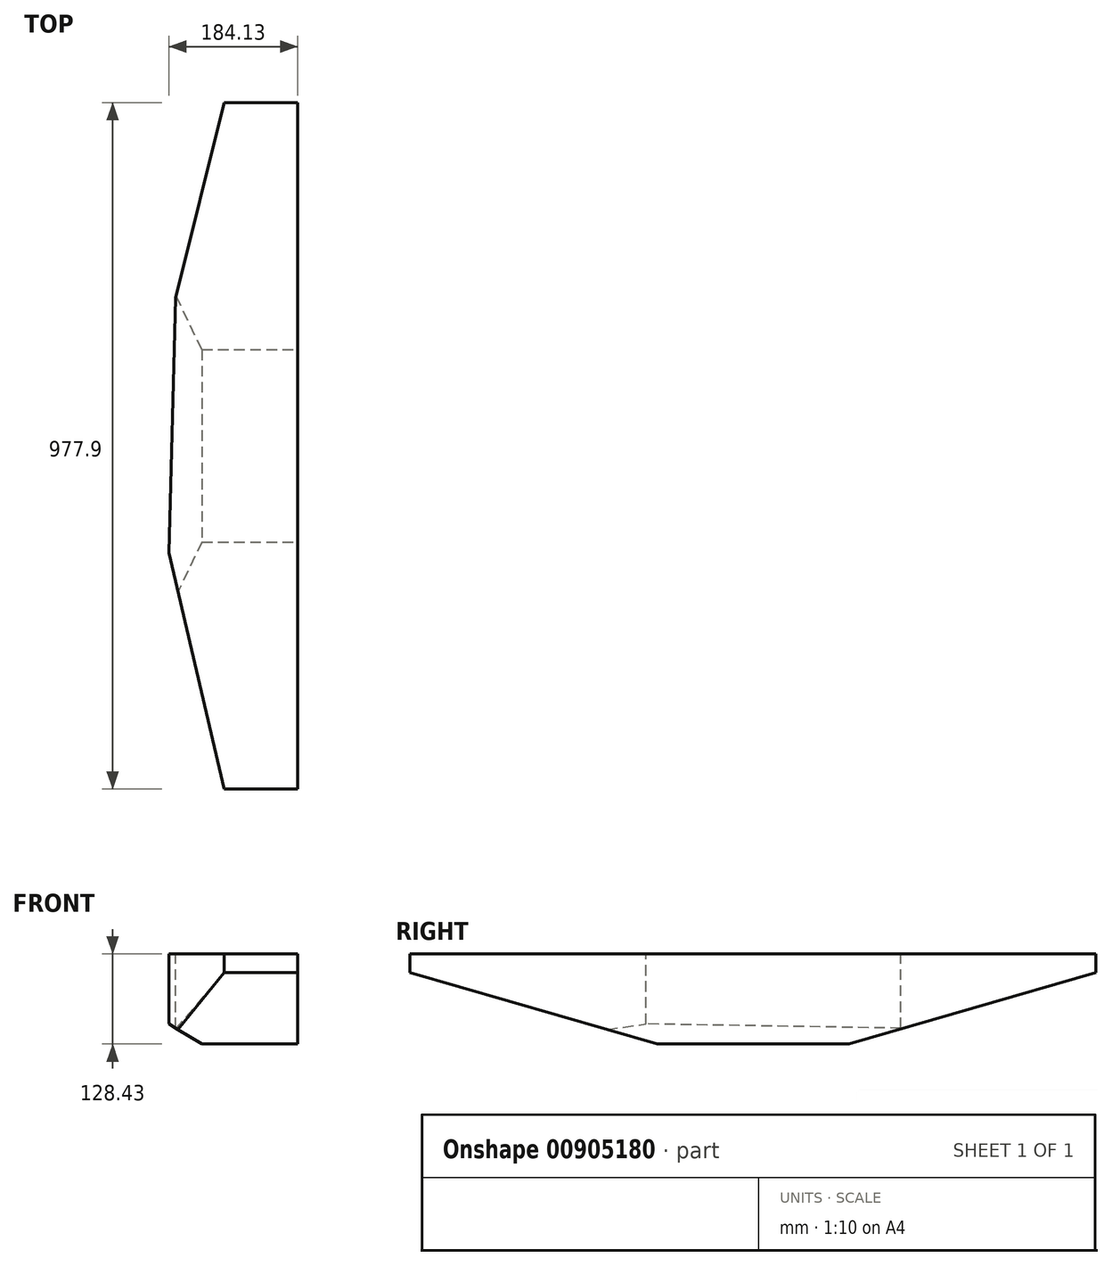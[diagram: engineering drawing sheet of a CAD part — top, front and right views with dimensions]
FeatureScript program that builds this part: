
annotation { "Feature Type Name" : "Feature", "Feature Type Description" : "" }
export const myFeature = defineFeature(function(context is Context, id is Id, definition is map)
    precondition{}
    {
        {
            var Q0;
            Q0=qCreatedBy(makeId("Front.planeOp"),FACE);
            var sketch = newSketch(context, id + "F0", { "sketchPlane" : qUnion([Q0])});
            skLineSegment(sketch, "E0", {"start": v(0, 0) * mm, "end": v(-306, 0) * mm});
            skLineSegment(sketch, "E1", {"start": v(-306, 0) * mm, "end": v(-306, 128.43) * mm});
            skLineSegment(sketch, "E2", {"start": v(-306, 128.43) * mm, "end": v(0, 128.43) * mm});
            skLineSegment(sketch, "E3", {"start": v(0, 128.43) * mm, "end": v(0, 0) * mm});
            skSolve(sketch);
        }
        {
            var Q0;
            Q0 = qSketchRegion(id + "F0", true);
            extrude(context, id + "F1", {"entities" : qUnion([Q0]), "depth" : 977.9 * mm, "offsetDistance" : 25.4 * mm});
        }
        {
            var Q0;
            Q0=makeQuery(id+"F1.opExtrude","SWEPT_FACE",FACE,{"disambiguationData":[OSD([sQuery(id+"F0.wireOp",EDGE,"E3")])]});
            var sketch = newSketch(context, id + "F2", { "sketchPlane" : qUnion([Q0])});
            skLineSegment(sketch, "E4", {"start": v(-977.9, 102.12) * mm, "end": v(-625.85, 0) * mm});
            skLineSegment(sketch, "E5", {"start": v(-625.85, 0) * mm, "end": v(-977.9, 0) * mm});
            skLineSegment(sketch, "E6", {"start": v(-977.9, 0) * mm, "end": v(-977.9, 102.12) * mm});
            skLineSegment(sketch, "E7", {"start": v(0, 0) * mm, "end": v(0, 102.12) * mm});
            skLineSegment(sketch, "E8", {"start": v(0, 102.12) * mm, "end": v(-352.04, 0) * mm});
            skLineSegment(sketch, "E9", {"start": v(-352.04, 0) * mm, "end": v(0, 0) * mm});
            skSolve(sketch);
        }
        {
            var Q0;
            Q0 = qSketchRegion(id + "F2", true);
            extrude(context, id + "F3", {"entities" : qUnion([Q0]), "operationType" : NewBodyOperationType.REMOVE, "oppositeDirection" : true, "depth" : 508 * mm, "offsetDistance" : 25.4 * mm});
        }
        {
            var Q0;
            Q0=makeQuery(id+"F1.opExtrude","CAP_FACE",FACE,{"disambiguationData":[OSD([sQuery(id+"F0.wireOp",EDGE,"E0"),sQuery(id+"F0.wireOp",EDGE,"E1"),sQuery(id+"F0.wireOp",EDGE,"E2"),sQuery(id+"F0.wireOp",EDGE,"E3")])],"isStart":false});
            var sketch = newSketch(context, id + "F4", { "sketchPlane" : qUnion([Q0])});
            skLineSegment(sketch, "E10", {"start": v(-306, 102.12) * mm, "end": v(-306, 0) * mm});
            skLineSegment(sketch, "E11", {"start": v(-306, 0) * mm, "end": v(-136.76, 0) * mm});
            skLineSegment(sketch, "E12", {"start": v(-136.76, 0) * mm, "end": v(-306, 102.12) * mm});
            skSolve(sketch);
        }
        {
            var Q0;
            Q0 = qSketchRegion(id + "F4", true);
            extrude(context, id + "F5", {"entities" : qUnion([Q0]), "operationType" : NewBodyOperationType.REMOVE, "oppositeDirection" : true, "depth" : 1577.34 * mm, "offsetDistance" : 25.4 * mm});
        }
        {
            var Q0;
            Q0=makeQuery(id+"F1.opExtrude","CAP_FACE",FACE,{"disambiguationData":[OSD([sQuery(id+"F0.wireOp",EDGE,"E0"),sQuery(id+"F0.wireOp",EDGE,"E1"),sQuery(id+"F0.wireOp",EDGE,"E2"),sQuery(id+"F0.wireOp",EDGE,"E3")])],"isStart":true});
            var sketch = newSketch(context, id + "F6", { "sketchPlane" : qUnion([Q0])});
            skLineSegment(sketch, "E13", {"start": v(209.7, 128.43) * mm, "end": v(209.7, 102.12) * mm});
            skLineSegment(sketch, "E14", {"start": v(209.7, 102.12) * mm, "end": v(306, 102.12) * mm});
            skLineSegment(sketch, "E15", {"start": v(306, 102.12) * mm, "end": v(306, 128.43) * mm});
            skLineSegment(sketch, "E16", {"start": v(306, 128.43) * mm, "end": v(209.7, 128.43) * mm});
            skSolve(sketch);
        }
        {
            var Q0;
            Q0 = qSketchRegion(id + "F6", true);
            extrude(context, id + "F7", {"entities" : qUnion([Q0]), "operationType" : NewBodyOperationType.REMOVE, "oppositeDirection" : true, "depth" : 2032 * mm, "offsetDistance" : 25.4 * mm});
        }
        {
            var Q0;
            Q0=makeQuery(id+"F1.opExtrude","SWEPT_FACE",FACE,{"disambiguationData":[OSD([sQuery(id+"F0.wireOp",EDGE,"E2")])]});
            var sketch = newSketch(context, id + "F8", { "sketchPlane" : qUnion([Q0])});
            skLineSegment(sketch, "E17", {"start": v(-104.85, 0) * mm, "end": v(-310.77, -826.15) * mm});
            skLineSegment(sketch, "E18", {"start": v(-310.77, -826.15) * mm, "end": v(-310.77, 0) * mm});
            skLineSegment(sketch, "E19", {"start": v(-310.77, 0) * mm, "end": v(-104.85, 0) * mm});
            skLineSegment(sketch, "E20", {"start": v(-104.85, -977.9) * mm, "end": v(-310.77, -104.12) * mm});
            skLineSegment(sketch, "E21", {"start": v(-310.77, -104.12) * mm, "end": v(-310.77, -977.9) * mm});
            skLineSegment(sketch, "E22", {"start": v(-310.77, -977.9) * mm, "end": v(-104.85, -977.9) * mm});
            skSolve(sketch);
        }
        {
            var Q0;
            Q0 = qSketchRegion(id + "F8", true);
            extrude(context, id + "F9", {"entities" : qUnion([Q0]), "operationType" : NewBodyOperationType.REMOVE, "oppositeDirection" : true, "depth" : 2032 * mm, "offsetDistance" : 25.4 * mm});
        }
        {
            var Q0;
            Q0=makeQuery(id+"F1.opExtrude","SWEPT_FACE",FACE,{"disambiguationData":[OSD([sQuery(id+"F0.wireOp",EDGE,"E2")])]});
            var sketch = newSketch(context, id + "F10", { "sketchPlane" : qUnion([Q0])});
            skLineSegment(sketch, "E23", {"start": v(-174.2, -278.18) * mm, "end": v(-184.13, -641.52) * mm});
            skLineSegment(sketch, "E24", {"start": v(-184.13, -641.52) * mm, "end": v(-476.84, -662.85) * mm});
            skLineSegment(sketch, "E25", {"start": v(-476.84, -662.85) * mm, "end": v(-174.2, -278.18) * mm});
            skSolve(sketch);
        }
        {
            var Q0;
            Q0 = qSketchRegion(id + "F10", true);
            extrude(context, id + "F11", {"entities" : qUnion([Q0]), "operationType" : NewBodyOperationType.REMOVE, "oppositeDirection" : true, "depth" : 2032 * mm, "offsetDistance" : 25.4 * mm});
        }
    });
